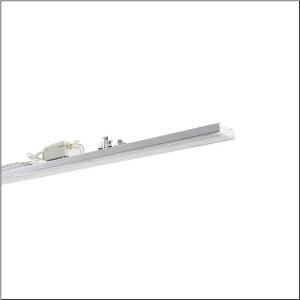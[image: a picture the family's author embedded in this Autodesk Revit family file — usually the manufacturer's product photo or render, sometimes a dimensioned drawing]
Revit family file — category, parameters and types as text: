
# Revit family: licross_r__21_recessed_mo_52tl18dn495g_5e12
name_source: partatom
category: Lighting Fixtures
units: mm (PartAtom-declared; Revit-internal decimal feet)

## family parameters
Cut with Voids When Loaded = No
Host = Face
Light Source = No
Part Type = Normal
Room Calculation Point = No
Round Connector Dimension = Use Diameter
Shared = No

## types (1)
- --- (1 x LED, 9990 lm, 58 W, 4000K)
    Apparent Load = 58 VA
    CIE Flux Codes = 79 95 99 100 100
    Color Rendering = 80
    Color Temperature = 4000K
    Default Elevation = 1800 mm
    Description = Licross® 21 Recessed MO, luminaire insert, of sheet steel, galvanised, coil coated, white, length: 1.500mm, width: 66mm, height: 67mm, LED rated luminous flux: 9.990lm, light colour: 840, control gear: DALI 2, with plug, 5-pole, with phase selection, mains connection: 220..240V, AC, 50/60Hz, rated input power: 58W, halogen-free wiring, primary light control with lens, of plastic, primary optical cover: cover, of PMMA, light emission: direct distribution, primary light characteristic: symmetric, protection rating (complete): IP40, insulation class (complete): insulation class I (protective earthing), certification: CE, ENEC, VDE, UKCA, protection symbol: D if used in an environment without relevant dust loads with corresponding accessories, impact resistance: IK06, permissible ambient temperature for indoor applications: -25..+35°C, corresponds to IFS (International Featured Standards) requirements for safety and quality in the food industry, reducing of maximum allowable ambient temperature of 5°C with ceiling mounting, LABS conformity tested according to VDMA 24364:2018-05, packaging unit: 1 piece
    Height = 58 mm
    Lamp = 1 x LED
    Lamp Light Flux = 9990 lm
    Lamp Power = 58 W
    Lamp count = 1
    Length = 1500 mm
    Luminous efficacy = 172 lm/W
    Manufacturer = Siteco
    ModVariant = No
    Model = 52TL18DN495G
    Mounting Place = Ceiling
    Mounting Type = Pendant
    Number of Poles = 1
    OnlyDefault = Yes
    Power Factor = 1
    Product Name = Licross® 21 Recessed MO
    Product group = luminaire insert
    ProductGroupID = 901
    Protection Class = Protection class I
    Protection Degree = IP 40
    RLX_Detail_Level = 1
    RLX_Emergency_Light_Flux = 0 lm
    RLX_Emergency_Type = 0
    RLX_Emergency_Type_DB = No
    RlxData = <blob elided: 24485 chars, md5=c0cd4e78>
    Socket = socket
    Standby Power = 0 W
    System Light Flux = 9990 lm
    System Power = 58 W
    Type Comments = factory setting: luminous flux: 100 % | dim-lin: 254 | 390 mA
    Type Image = l_1296930.jpg
    URL = http://relux.com
    VarID = @adj_121236
    Voltage = 0 V
    Weight = 0.00 kg
    Width = 66 mm

## geometry (parser evidence)
native form markers: Blend x4, Sweep x11
no freeform markers — native parametric forms only
